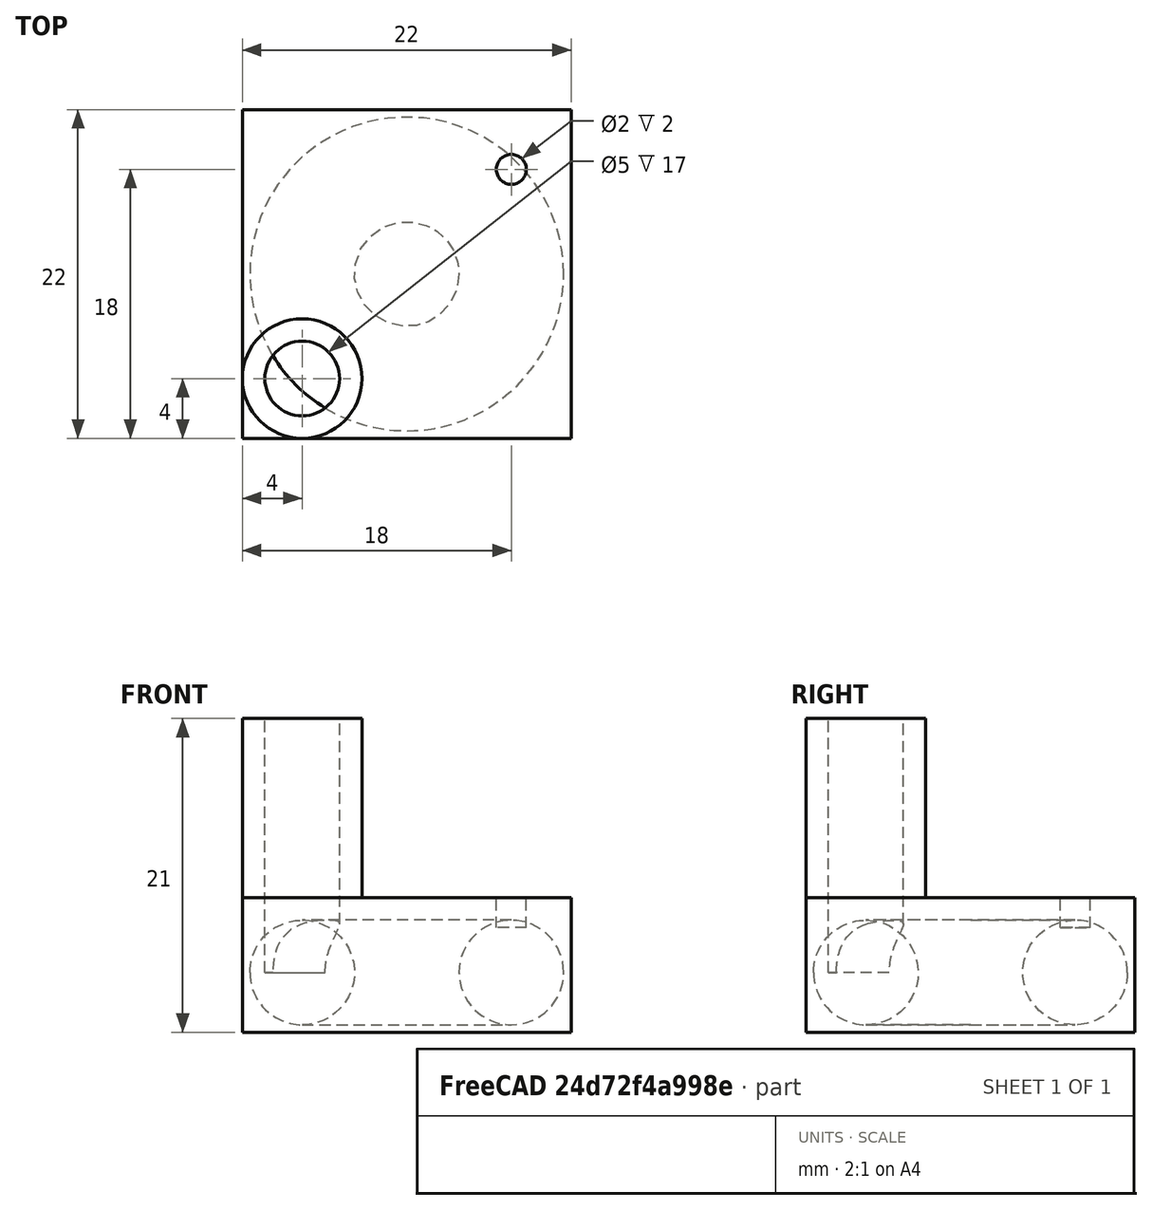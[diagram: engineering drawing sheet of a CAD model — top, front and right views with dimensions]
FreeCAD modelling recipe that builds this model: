
FCSTD DOCUMENT  (FreeCAD 0.17R13509 (Git))
Label: torus
License: All rights reserved
LicenseURL: http://en.wikipedia.org/wiki/All_rights_reserved
objects: Part::Cylinder×3, Part::MultiFuse×2, Part::Torus×1, Part::Box×1, Part::Cut×1
note: 8 computed .brp shape members not serialized (recipe doc carries the construction recipe); baked Part::Feature solids carry a one-line shape summary decoded from their .brp

FEATURE [Part::Torus] Torus
  Angle1 = -180
  Angle2 = 180
  Angle3 = 360
  AttacherType = Attacher::AttachEngine3D
  Placement = pos=(3,3,4) rot=(0,0,1;0rad)
  Radius1 = 7
  Radius2 = 3.5
FEATURE [Part::Box] Box  label="Cube"
  AttacherType = Attacher::AttachEngine3D
  Height = 9
  Length = 22
  Placement = pos=(-8,-8,0) rot=(0,0,1;0rad)
  Width = 22
FEATURE [Part::Cylinder] Cylinder
  Angle = 360
  AttacherType = Attacher::AttachEngine3D
  Height = 17
  Placement = pos=(-4,-4,4) rot=(0,0,1;0rad)
  Radius = 2.5
FEATURE [Part::Cylinder] Cylinder001
  Angle = 360
  AttacherType = Attacher::AttachEngine3D
  Height = 17
  Placement = pos=(-4,-4,4) rot=(0,0,1;0rad)
  Radius = 4
FEATURE [Part::MultiFuse] Fusion001
  Shapes = -> [Box,Cylinder001]
FEATURE [Part::Cylinder] Cylinder002
  Angle = 360
  AttacherType = Attacher::AttachEngine3D
  Height = 10
  Placement = pos=(10,10,7) rot=(0,0,1;0rad)
  Radius = 1
FEATURE [Part::MultiFuse] Fusion
  Shapes = -> [Cylinder,Torus,Cylinder002]
FEATURE [Part::Cut] Cut
  Base = -> Fusion001
  Tool = -> Fusion
